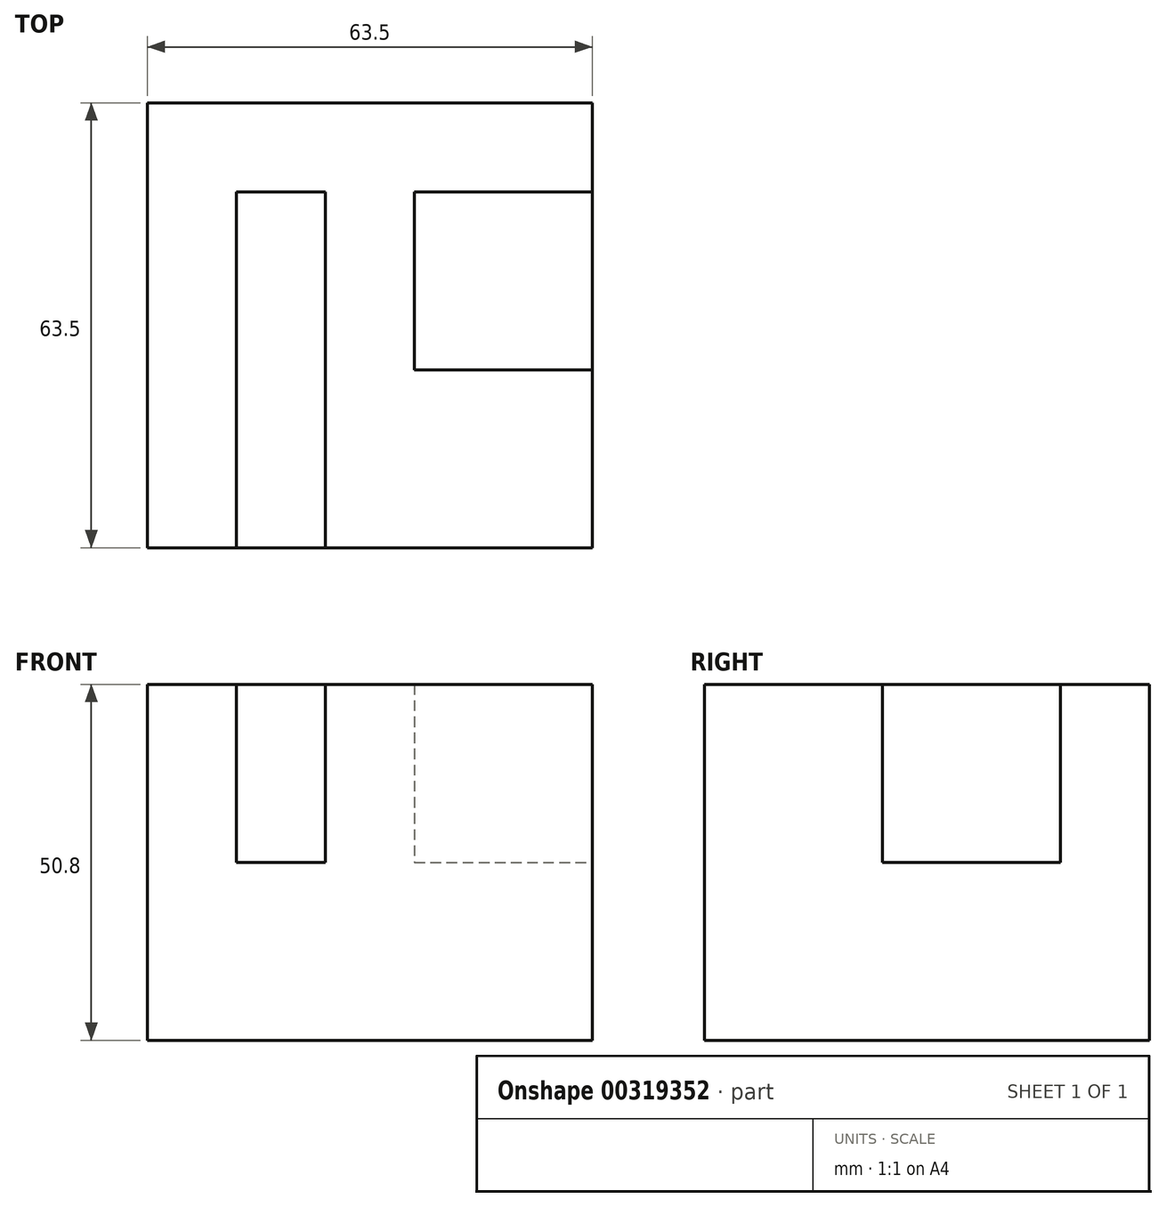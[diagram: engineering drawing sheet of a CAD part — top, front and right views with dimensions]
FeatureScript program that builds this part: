
annotation { "Feature Type Name" : "Feature", "Feature Type Description" : "" }
export const myFeature = defineFeature(function(context is Context, id is Id, definition is map)
    precondition{}
    {
        {
            var Q0;
            Q0=qCreatedBy(makeId("Front.planeOp"),FACE);
            var sketch = newSketch(context, id + "F0", { "sketchPlane" : qUnion([Q0])});
            skLineSegment(sketch, "E0", {"start": v(-45.4, 27.71) * mm, "end": v(18.1, 27.71) * mm});
            skLineSegment(sketch, "E1", {"start": v(18.1, 27.71) * mm, "end": v(18.1, -23.09) * mm});
            skLineSegment(sketch, "E2", {"start": v(18.1, -23.09) * mm, "end": v(-45.4, -23.09) * mm});
            skLineSegment(sketch, "E3", {"start": v(-45.4, -23.09) * mm, "end": v(-45.4, 27.71) * mm});
            skSolve(sketch);
        }
        {
            var Q0;
            Q0=makeQuery(id+"F0.imprint","IMPRINT",FACE,{"disambiguationData":[TD([[makeQuery(id+"F0.imprint","IMPRINT",EDGE,{"derivedFrom":sQuery(id+"F0.wireOp",EDGE,"E0")}),-1.0]])]});
            extrude(context, id + "F1", {"entities" : qUnion([Q0]), "depth" : 63.5 * mm});
        }
        {
            var Q0;
            Q0=makeQuery(id+"F1.opExtrude","CAP_FACE",FACE,{"disambiguationData":[OSD([sQuery(id+"F0.wireOp",EDGE,"E0"),sQuery(id+"F0.wireOp",EDGE,"E1"),sQuery(id+"F0.wireOp",EDGE,"E2"),sQuery(id+"F0.wireOp",EDGE,"E3")])],"isStart":false});
            var sketch = newSketch(context, id + "F2", { "sketchPlane" : qUnion([Q0])});
            skLineSegment(sketch, "E4.bottom", {"start": v(-32.7, 27.71) * mm, "end": v(-20, 27.71) * mm});
            skLineSegment(sketch, "E4.top", {"start": v(-32.7, 2.31) * mm, "end": v(-20, 2.31) * mm});
            skLineSegment(sketch, "E4.left", {"start": v(-32.7, 27.71) * mm, "end": v(-32.7, 2.31) * mm});
            skLineSegment(sketch, "E4.right", {"start": v(-20, 27.71) * mm, "end": v(-20, 2.31) * mm});
            skSolve(sketch);
        }
        {
            var Q0;
            Q0=makeQuery(id+"F2.imprint","IMPRINT",FACE,{"disambiguationData":[TD([[makeQuery(id+"F2.imprint","IMPRINT",EDGE,{"derivedFrom":sQuery(id+"F2.wireOp",EDGE,"E4.bottom")}),-1.0]])]});
            extrude(context, id + "F3", {"entities" : qUnion([Q0]), "operationType" : NewBodyOperationType.REMOVE, "oppositeDirection" : true, "depth" : 50.8 * mm});
        }
        {
            var Q0;
            Q0=makeQuery(id+"F1.opExtrude","SWEPT_FACE",FACE,{"disambiguationData":[OSD([sQuery(id+"F0.wireOp",EDGE,"E1")])]});
            var sketch = newSketch(context, id + "F4", { "sketchPlane" : qUnion([Q0])});
            skLineSegment(sketch, "E5.bottom", {"start": v(-12.7, 27.71) * mm, "end": v(-38.1, 27.71) * mm});
            skLineSegment(sketch, "E5.top", {"start": v(-12.7, 2.31) * mm, "end": v(-38.1, 2.31) * mm});
            skLineSegment(sketch, "E5.left", {"start": v(-12.7, 27.71) * mm, "end": v(-12.7, 2.31) * mm});
            skLineSegment(sketch, "E5.right", {"start": v(-38.1, 27.71) * mm, "end": v(-38.1, 2.31) * mm});
            skSolve(sketch);
        }
        {
            var Q0;
            Q0=makeQuery(id+"F4.imprint","IMPRINT",FACE,{"disambiguationData":[TD([[makeQuery(id+"F4.imprint","IMPRINT",EDGE,{"derivedFrom":sQuery(id+"F4.wireOp",EDGE,"E5.bottom")}),-1.0]])]});
            extrude(context, id + "F5", {"entities" : qUnion([Q0]), "operationType" : NewBodyOperationType.REMOVE, "oppositeDirection" : true, "depth" : 25.4 * mm});
        }
    });
